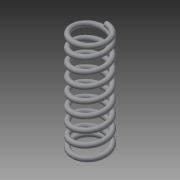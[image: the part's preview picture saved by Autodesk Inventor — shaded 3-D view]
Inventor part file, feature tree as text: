
AUTODESK INVENTOR PART (.ipt)
format: ipt  version: 2013 (Build 170138000, 138)  size: 493,056 bytes
history: native  units: mm
features: helix x1, sketch x1
ambient origin geometry x8: Origin, YZ Plane, XZ Plane, XY Plane, X Axis, Y Axis, Z Axis, Center Point
bodies: Solid1 (feature_tree)
feature tree (2):
  helix  "Coil1"  [1 undecoded]
  sketch  "Sketch1"  dims[d2=2.38125mm d3=10.0mm d4=12.7mm d5=70.0mm d6=0.0mm d7=270.0deg d8=90.0deg d9=270.0deg d10=90.0deg]
note: 1 required parameter value undecoded (feature->parameter linkage not recoverable at this tier; creation-order binding heuristic only, values carry confidence <= 0.55)
